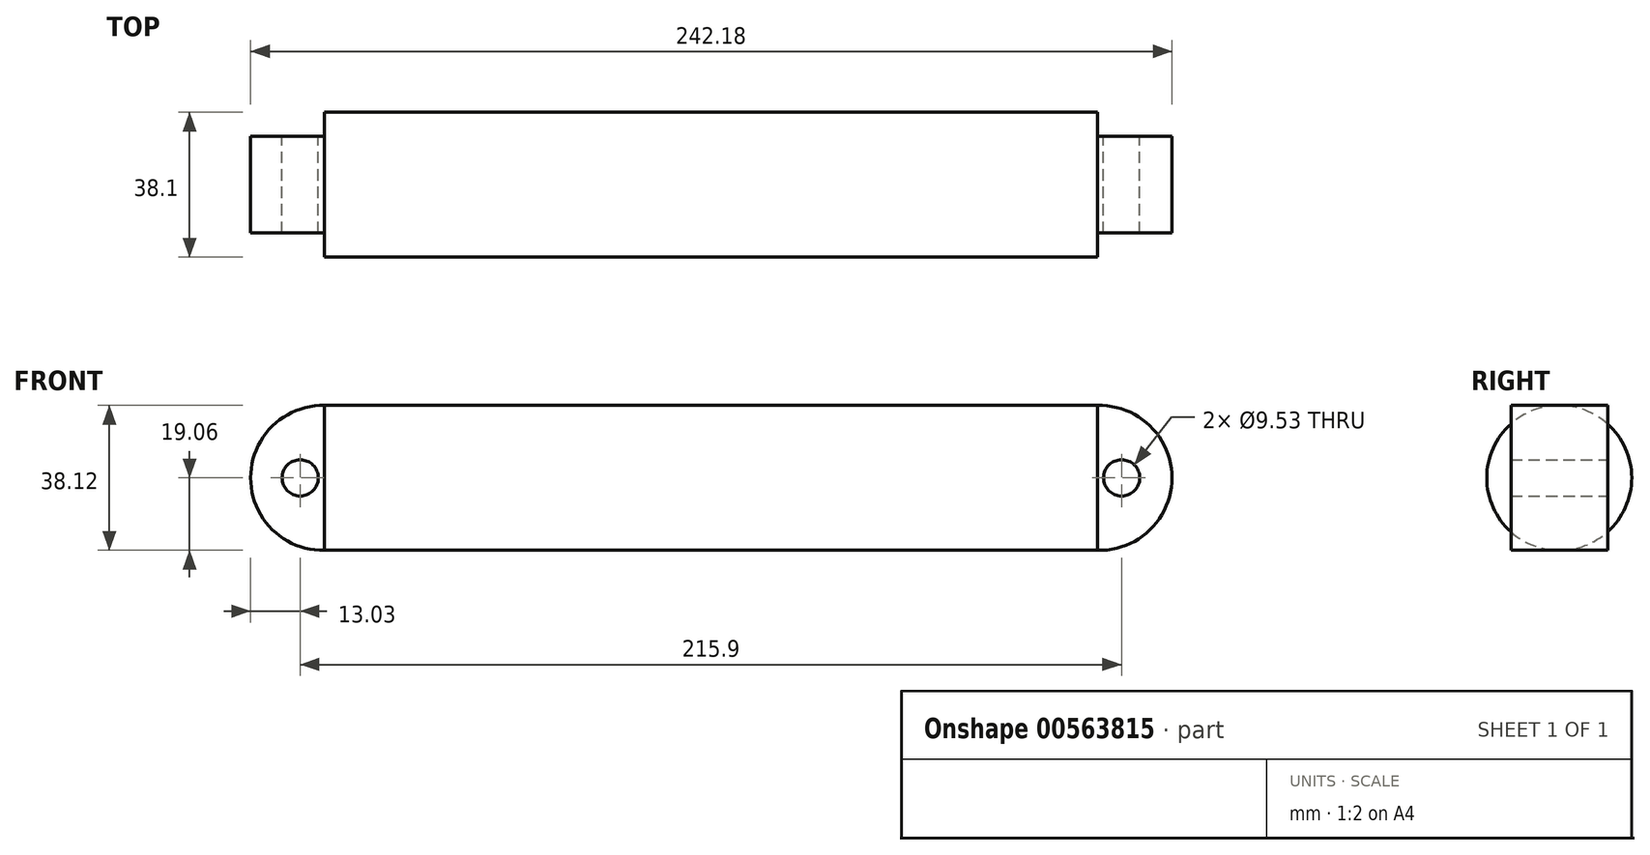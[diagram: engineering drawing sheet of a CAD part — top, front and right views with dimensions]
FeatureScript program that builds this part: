
annotation { "Feature Type Name" : "Feature", "Feature Type Description" : "" }
export const myFeature = defineFeature(function(context is Context, id is Id, definition is map)
    precondition{}
    {
        {
            var Q0;
            Q0=qCreatedBy(makeId("Front.planeOp"),FACE);
            var sketch = newSketch(context, id + "F0", { "sketchPlane" : qUnion([Q0])});
            skLineSegment(sketch, "E0.bottom", {"start": v(-101.6, 19.05) * mm, "end": v(101.6, 19.05) * mm});
            skLineSegment(sketch, "E0.top", {"start": v(-101.6, -19.05) * mm, "end": v(101.6, -19.05) * mm});
            skLineSegment(sketch, "E0.left", {"start": v(-101.6, 19.05) * mm, "end": v(-101.6, -19.05) * mm});
            skLineSegment(sketch, "E0.right", {"start": v(101.6, 19.05) * mm, "end": v(101.6, -19.05) * mm});
            skPoint(sketch, "E0.middle", {"position": v(0, 0) * mm});
            skSolve(sketch);
        }
        {
            var Q0;
            Q0=makeQuery(id+"F0.imprint","IMPRINT",FACE,{"disambiguationData":[TD([[makeQuery(id+"F0.imprint","IMPRINT",EDGE,{"derivedFrom":sQuery(id+"F0.wireOp",EDGE,"E0.bottom")}),-1.0]])]});
            extrude(context, id + "F1", {"entities" : qUnion([Q0]), "endBound" : BoundingType.SYMMETRIC, "depth" : 38.1 * mm, "offsetDistance" : 25.4 * mm});
        }
        {
            var Q0;
            Q0=makeQuery(id+"F1.opExtrude","CAP_EDGE",EDGE,{"disambiguationData":[OSD([sQuery(id+"F0.wireOp",EDGE,"E0.bottom")])],"isStart":false});
            var Q1;
            Q1=makeQuery(id+"F1.opExtrude","CAP_EDGE",EDGE,{"disambiguationData":[OSD([sQuery(id+"F0.wireOp",EDGE,"E0.bottom")])],"isStart":true});
            var Q2;
            Q2=makeQuery(id+"F1.opExtrude","CAP_EDGE",EDGE,{"disambiguationData":[OSD([sQuery(id+"F0.wireOp",EDGE,"E0.top")])],"isStart":true});
            var Q3;
            Q3=makeQuery(id+"F1.opExtrude","CAP_EDGE",EDGE,{"disambiguationData":[OSD([sQuery(id+"F0.wireOp",EDGE,"E0.top")])],"isStart":false});
            fillet(context, id + "F2", {"entities" : qUnion([Q0, Q1, Q2, Q3]), "radius" : 19.05 * mm, "tangentPropagation" : true, "allowEdgeOverflow" : false});
        }
        {
            var Q0;
            Q0=qCreatedBy(makeId("Front.planeOp"),FACE);
            var sketch = newSketch(context, id + "F3", { "sketchPlane" : qUnion([Q0])});
            skLineSegment(sketch, "E1", {"start": v(0, 0) * mm, "end": v(-101.6, 0) * mm});
            skLineSegment(sketch, "E2", {"start": v(-101.6, 0) * mm, "end": v(-101.6, 19.05) * mm});
            skLineSegment(sketch, "E3", {"start": v(-101.6, 19.05) * mm, "end": v(-101.6, -19.05) * mm});
            skArc(sketch, "E4", {"start": v(-101.6, 19.05) * mm, "mid": v(-120.98, 0) * mm, "end": v(-101.6, -19.05) * mm});
            skLineSegment(sketch, "E5", {"start": v(0, 0) * mm, "end": v(101.6, 0) * mm});
            skLineSegment(sketch, "E6", {"start": v(101.6, 0) * mm, "end": v(101.6, 19.05) * mm});
            skLineSegment(sketch, "E7", {"start": v(101.6, 19.05) * mm, "end": v(101.6, -19.05) * mm});
            skArc(sketch, "E8", {"start": v(101.6, -19.05) * mm, "mid": v(121.2, 0) * mm, "end": v(101.6, 19.05) * mm});
            skSolve(sketch);
        }
        {
            var Q0;
            {var subQ2=sQuery(id+"F3.wireOp",EDGE,"E4");Q0=makeQuery(id+"F3.imprint","IMPRINT",FACE,{"disambiguationData":[TD([[makeQuery(id+"F3.imprint","IMPRINT",EDGE,{"derivedFrom":subQ2}),1.0]])]});}
            var Q1;
            {var subQ2=sQuery(id+"F3.wireOp",EDGE,"E8");Q1=makeQuery(id+"F3.imprint","IMPRINT",FACE,{"disambiguationData":[TD([[makeQuery(id+"F3.imprint","IMPRINT",EDGE,{"derivedFrom":subQ2}),1.0]])]});}
            extrude(context, id + "F4", {"entities" : qUnion([Q0, Q1]), "operationType" : NewBodyOperationType.ADD, "endBound" : BoundingType.SYMMETRIC, "depth" : 25.4 * mm, "offsetDistance" : 25.4 * mm});
        }
        {
            var Q0;
            Q0=qCreatedBy(makeId("Front.planeOp"),FACE);
            var sketch = newSketch(context, id + "F5", { "sketchPlane" : qUnion([Q0])});
            skLineSegment(sketch, "E9", {"start": v(0, 0) * mm, "end": v(-107.95, 0) * mm});
            skLineSegment(sketch, "E10", {"start": v(0, 0) * mm, "end": v(107.95, 0) * mm});
            skCircle(sketch, "E11", {"center": v(-107.95, 0) * mm, "radius": 4.76 * mm});
            skCircle(sketch, "E12", {"center": v(107.95, 0) * mm, "radius": 4.76 * mm});
            skSolve(sketch);
        }
        {
            var Q0;
            Q0 = qSketchRegion(id + "F5", true);
            extrude(context, id + "F6", {"entities" : qUnion([Q0]), "operationType" : NewBodyOperationType.REMOVE, "endBound" : BoundingType.SYMMETRIC, "depth" : 25.4 * mm, "offsetDistance" : 25.4 * mm});
        }
    });
